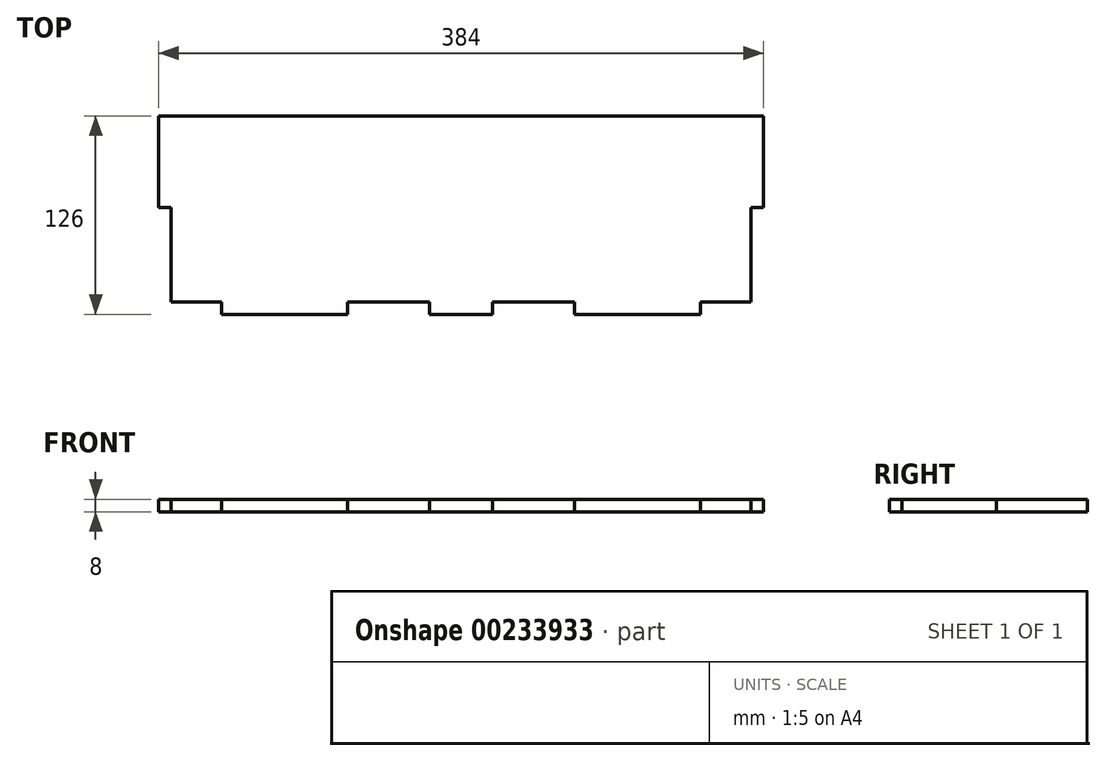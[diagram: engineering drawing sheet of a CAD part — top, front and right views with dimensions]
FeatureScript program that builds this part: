
annotation { "Feature Type Name" : "Feature", "Feature Type Description" : "" }
export const myFeature = defineFeature(function(context is Context, id is Id, definition is map)
    precondition{}
    {
        {
            var Q0;
            Q0=qCreatedBy(makeId("Top.planeOp"),FACE);
            var sketch = newSketch(context, id + "F0", { "sketchPlane" : qUnion([Q0])});
            skLineSegment(sketch, "E0", {"start": v(0, 0) * mm, "end": v(8, 0) * mm});
            skLineSegment(sketch, "E1", {"start": v(8, 0) * mm, "end": v(8, -60) * mm});
            skLineSegment(sketch, "E2", {"start": v(8, -60) * mm, "end": v(40, -60) * mm});
            skLineSegment(sketch, "E3", {"start": v(40, -60) * mm, "end": v(40, -68) * mm});
            skLineSegment(sketch, "E4", {"start": v(40, -68) * mm, "end": v(120, -68) * mm});
            skLineSegment(sketch, "E5", {"start": v(120, -68) * mm, "end": v(120, -60) * mm});
            skLineSegment(sketch, "E6", {"start": v(264, -60) * mm, "end": v(264, -68) * mm});
            skPoint(sketch, "E6.endSnap0", {"position": v(80, -68) * mm});
            skLineSegment(sketch, "E7", {"start": v(264, -68) * mm, "end": v(344, -68) * mm});
            skLineSegment(sketch, "E8", {"start": v(344, -68) * mm, "end": v(344, -60) * mm});
            skLineSegment(sketch, "E9", {"start": v(344, -60) * mm, "end": v(376, -60) * mm});
            skLineSegment(sketch, "E10", {"start": v(376, -60) * mm, "end": v(376, 0) * mm});
            skLineSegment(sketch, "E11", {"start": v(376, 0) * mm, "end": v(384, 0) * mm});
            skLineSegment(sketch, "E12", {"start": v(384, 0) * mm, "end": v(384, 58) * mm});
            skLineSegment(sketch, "E13", {"start": v(384, 58) * mm, "end": v(0, 58) * mm});
            skLineSegment(sketch, "E14", {"start": v(0, 58) * mm, "end": v(0, 0) * mm});
            skLineSegment(sketch, "E15", {"start": v(120, -60) * mm, "end": v(172, -60) * mm});
            skLineSegment(sketch, "E16", {"start": v(172, -60) * mm, "end": v(172, -68) * mm});
            skLineSegment(sketch, "E17", {"start": v(172, -68) * mm, "end": v(212, -68) * mm});
            skLineSegment(sketch, "E18", {"start": v(212, -68) * mm, "end": v(212, -60) * mm});
            skLineSegment(sketch, "E19", {"start": v(212, -60) * mm, "end": v(264, -60) * mm});
            skSolve(sketch);
        }
        {
            var Q0;
            Q0=makeQuery(id+"F0.imprint","IMPRINT",FACE,{"disambiguationData":[TD([[makeQuery(id+"F0.imprint","IMPRINT",EDGE,{"derivedFrom":sQuery(id+"F0.wireOp",EDGE,"E0")}),1.0]])]});
            extrude(context, id + "F1", {"entities" : qUnion([Q0]), "depth" : 8 * mm});
        }
    });
